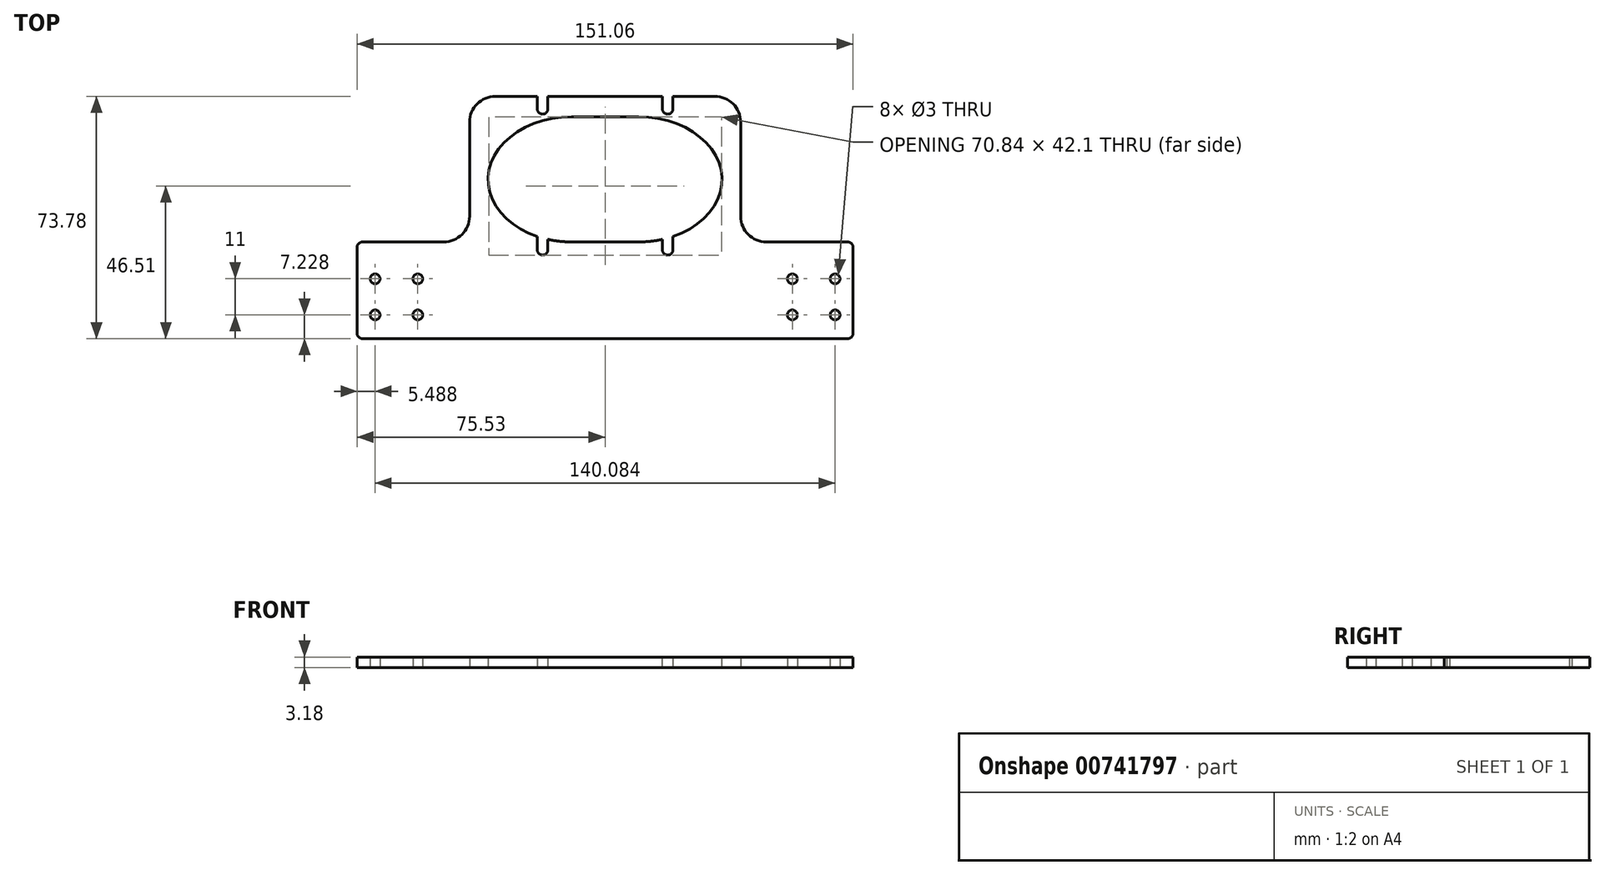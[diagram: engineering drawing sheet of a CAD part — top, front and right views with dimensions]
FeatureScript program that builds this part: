
annotation { "Feature Type Name" : "Feature", "Feature Type Description" : "" }
export const myFeature = defineFeature(function(context is Context, id is Id, definition is map)
    precondition{}
    {
        {
            var Q0;
            Q0=qCreatedBy(makeId("Top.planeOp"),FACE);
            var sketch = newSketch(context, id + "F0", { "sketchPlane" : qUnion([Q0])});
            skLineSegment(sketch, "E0", {"start": v(0, 44.32) * mm, "end": v(-33.46, 44.32) * mm});
            skLineSegment(sketch, "E1", {"start": v(-41.28, 36.5) * mm, "end": v(-41.28, 7.82) * mm});
            skLineSegment(sketch, "E2", {"start": v(-49.1, 0) * mm, "end": v(-73.88, 0) * mm});
            skLineSegment(sketch, "E3", {"start": v(-75.53, -1.65) * mm, "end": v(-75.53, -27.81) * mm});
            skLineSegment(sketch, "E4", {"start": v(-73.88, -29.46) * mm, "end": v(0, -29.46) * mm});
            skLineSegment(sketch, "E5", {"start": v(0, -29.46) * mm, "end": v(0, 0) * mm});
            skLineSegment(sketch, "E6", {"start": v(0, 0) * mm, "end": v(-10.23, 0) * mm});
            skLineSegment(sketch, "E7", {"start": v(-10.23, 38.1) * mm, "end": v(0, 38.1) * mm});
            skLineSegment(sketch, "E8", {"start": v(0, 38.1) * mm, "end": v(0, 44.32) * mm});
            skPoint(sketch, "E9.visualSharp", {"position": v(-41.28, 44.32) * mm});
            skArc(sketch, "E9.filletArc", {"start": v(-33.46, 44.32) * mm, "mid": v(-39, 42.03) * mm, "end": v(-41.28, 36.5) * mm});
            skPoint(sketch, "E10.visualSharp", {"position": v(-41.28, 0) * mm});
            skArc(sketch, "E10.filletArc", {"start": v(-49.1, 0) * mm, "mid": v(-43.58, 2.3) * mm, "end": v(-41.28, 7.82) * mm});
            skPoint(sketch, "E11.visualSharp", {"position": v(-75.53, 0) * mm});
            skArc(sketch, "E11.filletArc", {"start": v(-73.88, 0) * mm, "mid": v(-75.05, -0.48) * mm, "end": v(-75.53, -1.65) * mm});
            skPoint(sketch, "E12.visualSharp", {"position": v(-75.53, -29.46) * mm});
            skArc(sketch, "E12.filletArc", {"start": v(-75.53, -27.81) * mm, "mid": v(-75.05, -28.98) * mm, "end": v(-73.88, -29.46) * mm});
            skEllipticalArc(sketch, "E13", {});
            skCircle(sketch, "E14", {"center": v(-70.04, -22.23) * mm, "radius": 1.5 * mm});
            skCircle(sketch, "E15.0.1.0", {"center": v(-70.04, -11.23) * mm, "radius": 1.5 * mm});
            skCircle(sketch, "E15.1.0.0", {"center": v(-57.04, -22.23) * mm, "radius": 1.5 * mm});
            skCircle(sketch, "E15.1.1.0", {"center": v(-57.04, -11.23) * mm, "radius": 1.5 * mm});
            skLineSegment(sketch, "E15.direction1", {"start": v(-70.04, -22.23) * mm, "end": v(-57.04, -22.23) * mm, "construction": true});
            skLineSegment(sketch, "E15.direction2", {"start": v(-70.04, -22.23) * mm, "end": v(-70.04, -11.23) * mm, "construction": true});
            const initialGuessF0  = {"E13": [-0.010232, 0.01905, 1, 0, 0.0254, 0.01905, 1.5707963267948966, 4.71238898038469]};
            skSetInitialGuess(sketch, initialGuessF0);
            skSolve(sketch);
        }
        {
            var Q0;
            Q0 = qSketchRegion(id + "F0", true);
            extrude(context, id + "F1", {"entities" : qUnion([Q0]), "depth" : 3.17 * mm, "offsetDistance" : 25.4 * mm});
        }
        {
            var Q0;
            Q0=qCreatedBy(makeId("Top.planeOp"),FACE);
            var sketch = newSketch(context, id + "F2", { "sketchPlane" : qUnion([Q0])});
            skLineSegment(sketch, "E16.bottom", {"start": v(-20.64, 7.63) * mm, "end": v(-17.46, 7.63) * mm});
            skLineSegment(sketch, "E16.left", {"start": v(-20.64, 7.63) * mm, "end": v(-20.64, -2.41) * mm});
            skLineSegment(sketch, "E16.right", {"start": v(-17.46, 7.63) * mm, "end": v(-17.46, -2.41) * mm});
            skArc(sketch, "E17", {"start": v(-20.64, -2.41) * mm, "mid": v(-19.05, -4) * mm, "end": v(-17.46, -2.41) * mm});
            skArc(sketch, "E18.0.1.0", {"start": v(-20.64, 40.51) * mm, "mid": v(-19.05, 38.93) * mm, "end": v(-17.46, 40.51) * mm});
            skLineSegment(sketch, "E18.0.1.1", {"start": v(-20.64, 50.55) * mm, "end": v(-17.46, 50.55) * mm});
            skLineSegment(sketch, "E18.0.1.2", {"start": v(-17.46, 50.55) * mm, "end": v(-17.46, 40.51) * mm});
            skLineSegment(sketch, "E18.0.1.3", {"start": v(-20.64, 50.55) * mm, "end": v(-20.64, 40.51) * mm});
            skLineSegment(sketch, "E18.direction1", {"start": v(-20.64, -2.41) * mm, "end": v(14.28, -2.41) * mm, "construction": true});
            skLineSegment(sketch, "E18.direction2", {"start": v(-20.64, -2.41) * mm, "end": v(-20.64, 40.51) * mm, "construction": true});
            skSolve(sketch);
        }
        {
            var Q0;
            Q0=makeQuery(id+"F2.imprint","IMPRINT",FACE,{"disambiguationData":[TD([[makeQuery(id+"F2.imprint","IMPRINT",EDGE,{"derivedFrom":sQuery(id+"F2.wireOp",EDGE,"E18.0.1.0")}),1.0]])]});
            var Q1;
            Q1=makeQuery(id+"F2.imprint","IMPRINT",FACE,{"disambiguationData":[TD([[makeQuery(id+"F2.imprint","IMPRINT",EDGE,{"derivedFrom":sQuery(id+"F2.wireOp",EDGE,"E16.bottom")}),-1.0]])]});
            extrude(context, id + "F3", {"entities" : qUnion([Q0, Q1]), "operationType" : NewBodyOperationType.REMOVE, "endBound" : BoundingType.SYMMETRIC, "depth" : 25 * mm, "offsetDistance" : 25 * mm});
        }
        {
            var Q0;
            Q0=makeQuery(id+"F1.opExtrude","SWEPT_BODY",BODY,{"disambiguationData":[OSD([sQuery(id+"F0.wireOp",EDGE,"E0"),sQuery(id+"F0.wireOp",EDGE,"E1"),sQuery(id+"F0.wireOp",EDGE,"E2"),sQuery(id+"F0.wireOp",EDGE,"E3"),sQuery(id+"F0.wireOp",EDGE,"E4"),sQuery(id+"F0.wireOp",EDGE,"E5"),sQuery(id+"F0.wireOp",EDGE,"E6"),sQuery(id+"F0.wireOp",EDGE,"E7"),sQuery(id+"F0.wireOp",EDGE,"E8"),sQuery(id+"F0.wireOp",EDGE,"E9.filletArc"),sQuery(id+"F0.wireOp",EDGE,"E10.filletArc"),sQuery(id+"F0.wireOp",EDGE,"E11.filletArc"),sQuery(id+"F0.wireOp",EDGE,"E12.filletArc"),sQuery(id+"F0.wireOp",EDGE,"E13"),sQuery(id+"F0.wireOp",EDGE,"E14"),sQuery(id+"F0.wireOp",EDGE,"E15.0.1.0"),sQuery(id+"F0.wireOp",EDGE,"E15.1.0.0"),sQuery(id+"F0.wireOp",EDGE,"E15.1.1.0")])]});
            var Q1;
            Q1=qCreatedBy(makeId("Right.planeOp"),FACE);
            mirror(context, id + "F4", {"operationType" : NewBodyOperationType.ADD, "entities" : qUnion([Q0]), "mirrorPlane" : qUnion([Q1])});
        }
    });
